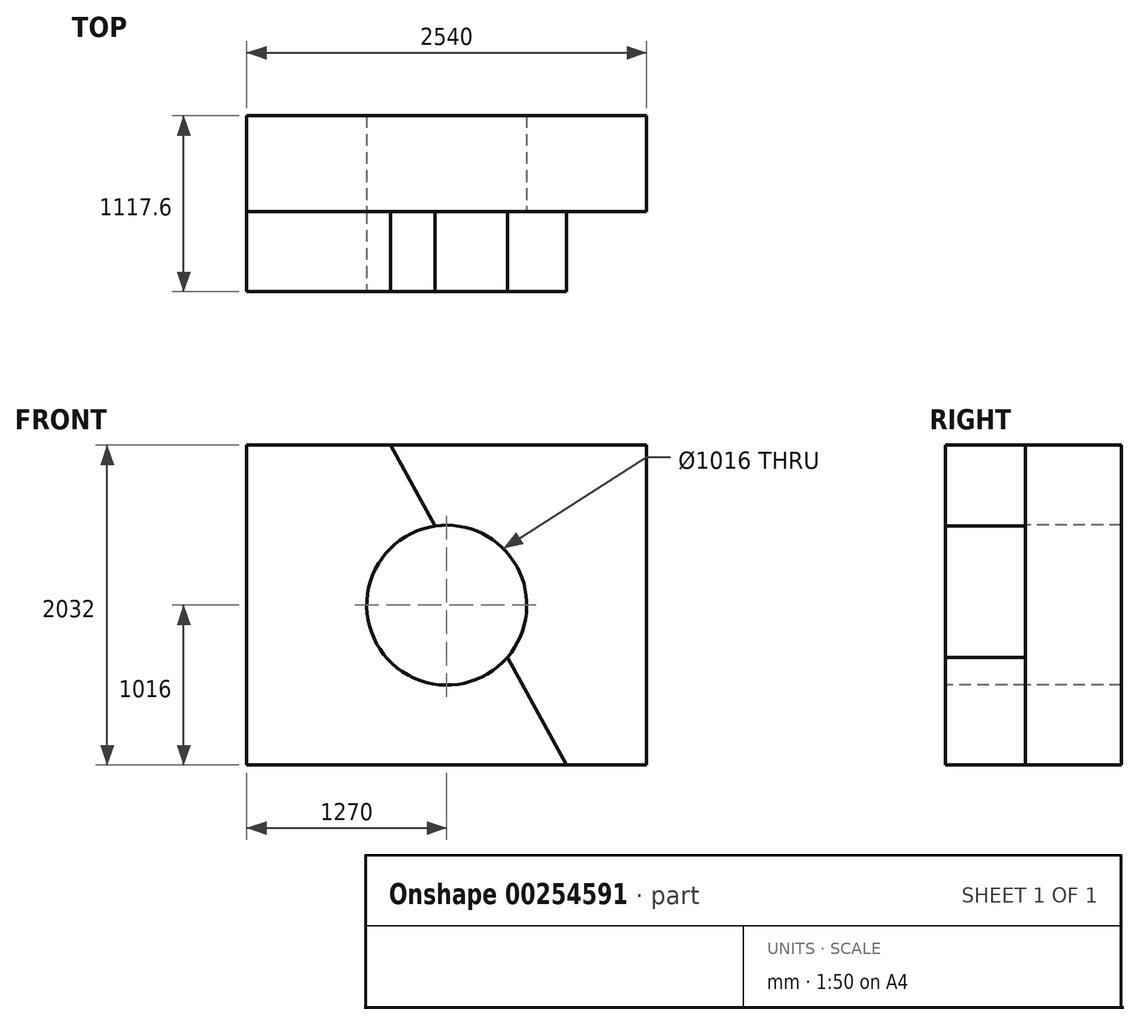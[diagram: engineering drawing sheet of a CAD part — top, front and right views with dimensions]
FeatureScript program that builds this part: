
annotation { "Feature Type Name" : "Feature", "Feature Type Description" : "" }
export const myFeature = defineFeature(function(context is Context, id is Id, definition is map)
    precondition{}
    {
        {
            var Q0;
            Q0=qCreatedBy(makeId("Front.planeOp"),FACE);
            var sketch = newSketch(context, id + "F0", { "sketchPlane" : qUnion([Q0])});
            skLineSegment(sketch, "E0.bottom", {"start": v(-1269.35, 1359.58) * mm, "end": v(1270.65, 1359.58) * mm});
            skLineSegment(sketch, "E0.top", {"start": v(-1269.35, -672.42) * mm, "end": v(1270.65, -672.42) * mm});
            skLineSegment(sketch, "E0.left", {"start": v(-1269.35, 1359.58) * mm, "end": v(-1269.35, -672.42) * mm});
            skLineSegment(sketch, "E0.right", {"start": v(1270.65, 1359.58) * mm, "end": v(1270.65, -672.42) * mm});
            skSolve(sketch);
        }
        {
            var Q0;
            Q0 = qSketchRegion(id + "F0", true);
            extrude(context, id + "F1", {"entities" : qUnion([Q0]), "depth" : 609.6 * mm});
        }
        {
            var Q0;
            Q0=makeQuery(id+"F1.opExtrude","CAP_FACE",FACE,{"disambiguationData":[OSD([sQuery(id+"F0.wireOp",EDGE,"E0.bottom"),sQuery(id+"F0.wireOp",EDGE,"E0.top"),sQuery(id+"F0.wireOp",EDGE,"E0.left"),sQuery(id+"F0.wireOp",EDGE,"E0.right")])],"isStart":false});
            var sketch = newSketch(context, id + "F2", { "sketchPlane" : qUnion([Q0])});
            skLineSegment(sketch, "E1", {"start": v(-1269.35, -672.42) * mm, "end": v(762.65, -672.42) * mm});
            skLineSegment(sketch, "E2", {"start": v(762.65, -672.42) * mm, "end": v(-354.95, 1359.58) * mm});
            skLineSegment(sketch, "E3", {"start": v(-354.95, 1359.58) * mm, "end": v(-1269.35, 1359.58) * mm});
            skLineSegment(sketch, "E4", {"start": v(-1269.35, 1359.58) * mm, "end": v(-1269.35, -672.42) * mm});
            skSolve(sketch);
        }
        {
            var Q0;
            Q0 = qSketchRegion(id + "F2", true);
            extrude(context, id + "F3", {"entities" : qUnion([Q0]), "depth" : 508 * mm});
        }
        {
            var Q0;
            Q0=makeQuery(id+"F3.opExtrude","CAP_FACE",FACE,{"disambiguationData":[OSD([sQuery(id+"F2.wireOp",EDGE,"E1"),sQuery(id+"F2.wireOp",EDGE,"E2"),sQuery(id+"F2.wireOp",EDGE,"E3"),sQuery(id+"F2.wireOp",EDGE,"E4")])],"isStart":false});
            var sketch = newSketch(context, id + "F4", { "sketchPlane" : qUnion([Q0])});
            skCircle(sketch, "E5", {"center": v(0.65, 343.58) * mm, "radius": 508 * mm});
            skSolve(sketch);
        }
        {
            var Q0;
            {var subQ0=sQuery(id+"F4.wireOp",EDGE,"E5");var subQ1=makeQuery(id+"F3.opExtrude","CAP_EDGE",EDGE,{"disambiguationData":[OSD([sQuery(id+"F2.wireOp",EDGE,"E2")])],"isStart":false});var subQ2=makeQuery(id+"F4.imprint","INTERSECT",VERTEX,{"disambiguationData":[OD(0.0)],"derivedFrom":[subQ1,subQ0]});Q0=makeQuery(id+"F4.imprint","IMPRINT",FACE,{"disambiguationData":[TD([[makeQuery(id+"F4.imprint","IMPRINT",EDGE,{"disambiguationData":[TD([[subQ2,1.0]])],"derivedFrom":subQ0}),1.0]])]});}
            var Q1;
            {var subQ0=sQuery(id+"F4.wireOp",EDGE,"E5");var subQ1=makeQuery(id+"F3.opExtrude","CAP_EDGE",EDGE,{"disambiguationData":[OSD([sQuery(id+"F2.wireOp",EDGE,"E2")])],"isStart":false});var subQ2=makeQuery(id+"F4.imprint","INTERSECT",VERTEX,{"disambiguationData":[OD(0.0)],"derivedFrom":[subQ1,subQ0]});Q1=makeQuery(id+"F4.imprint","IMPRINT",FACE,{"disambiguationData":[TD([[makeQuery(id+"F4.imprint","IMPRINT",EDGE,{"disambiguationData":[TD([[subQ2,-1.0]])],"derivedFrom":subQ0}),1.0]])]});}
            extrude(context, id + "F5", {"entities" : qUnion([Q0, Q1]), "operationType" : NewBodyOperationType.REMOVE, "oppositeDirection" : true, "depth" : 1117.6 * mm});
        }
    });
